# Revit family: FA_ХомутДляСтержняМачты_90536_EZETEK
name_source: partatom
category: Системы пожарной сигнализации
revit_build: Autodesk Revit 2017 (Build: 20160225_1515(x64)
units: mm (PartAtom-declared; Revit-internal decimal feet)

## family parameters
Всегда вертикально = Да
На основе рабочей плоскости = Нет
Общий = Да
При загрузке вырезать с полостями = Нет
Размер круглого соединителя = Использовать радиус
Сохранять ориентацию аннотаций = Нет
Тип детали = Нормальный
Точка расчета площади = Нет

## types (1)
- ХомутДляСтержняМачты_90536
    ADSK_Версия Revit = 2017
    ADSK_Единица измерения = шт.
    ADSK_Завод-изготовитель = Ezetek
    ADSK_Код изделия = 90536
    ADSK_Количество = 1
    ADSK_Марка = 90536
    ADSK_Масса = 0.04
    ADSK_Масса_Текст = 0.04
    ADSK_Материал = BIMLIB_Сталь_Нержавеющая_EZETEK
    ADSK_Наименование = Хомут для стержня 17-19 мм, нерж
    ADSK_Обозначение = 90536
    URL = https://ezetek.ru
    Группа модели = Хомуты
    Изготовитель = Ezetek
    Описание = Хомуты используются для соединения молниеприемника с прутком, либо мачты с прутком.
    Угол = 90.00°
